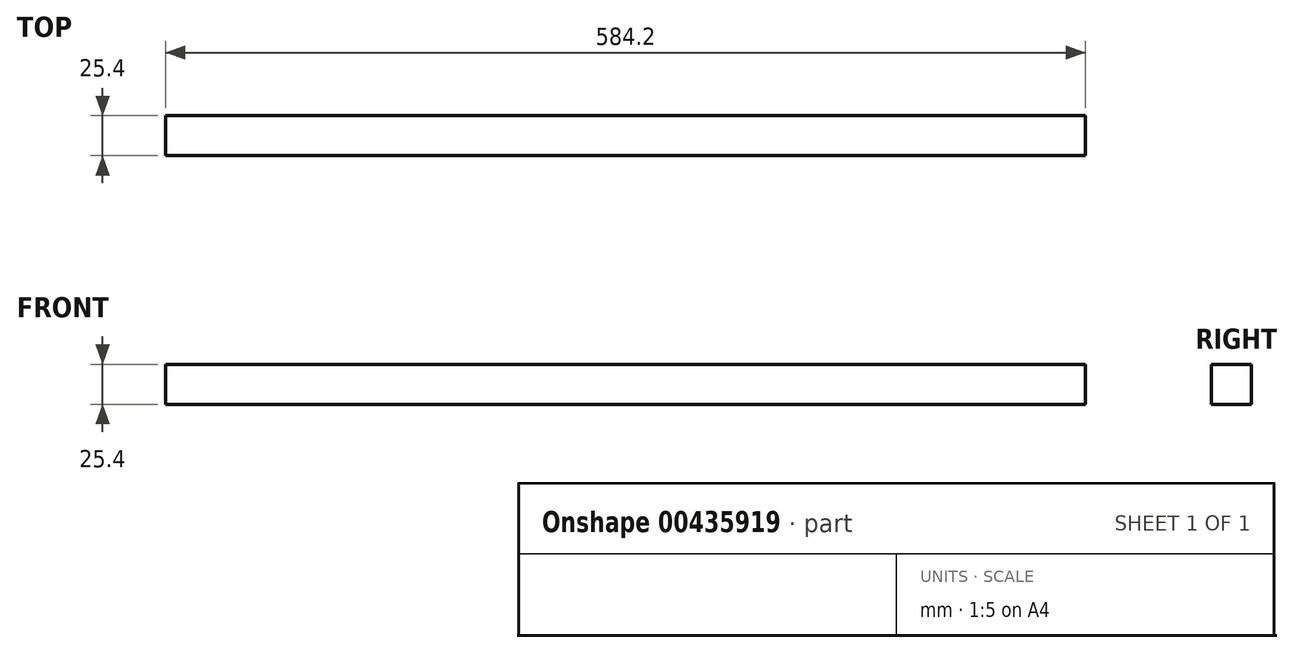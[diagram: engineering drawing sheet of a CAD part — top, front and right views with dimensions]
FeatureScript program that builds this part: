
annotation { "Feature Type Name" : "Feature", "Feature Type Description" : "" }
export const myFeature = defineFeature(function(context is Context, id is Id, definition is map)
    precondition{}
    {
        {
            var Q0;
            Q0=qCreatedBy(makeId("Right.planeOp"),FACE);
            var sketch = newSketch(context, id + "F0", { "sketchPlane" : qUnion([Q0])});
            skLineSegment(sketch, "E0.bottom", {"start": v(12.7, 12.7) * mm, "end": v(-12.7, 12.7) * mm});
            skLineSegment(sketch, "E0.top", {"start": v(12.7, -12.7) * mm, "end": v(-12.7, -12.7) * mm});
            skLineSegment(sketch, "E0.left", {"start": v(12.7, 12.7) * mm, "end": v(12.7, -12.7) * mm});
            skLineSegment(sketch, "E0.right", {"start": v(-12.7, 12.7) * mm, "end": v(-12.7, -12.7) * mm});
            skPoint(sketch, "E0.middle", {"position": v(0, 0) * mm});
            skSolve(sketch);
        }
        {
            var Q0;
            Q0=makeQuery(id+"F0.imprint","IMPRINT",FACE,{"disambiguationData":[TD([[makeQuery(id+"F0.imprint","IMPRINT",EDGE,{"derivedFrom":sQuery(id+"F0.wireOp",EDGE,"E0.bottom")}),1.0]])]});
            extrude(context, id + "F1", {"entities" : qUnion([Q0]), "depth" : 584.2 * mm});
        }
    });
